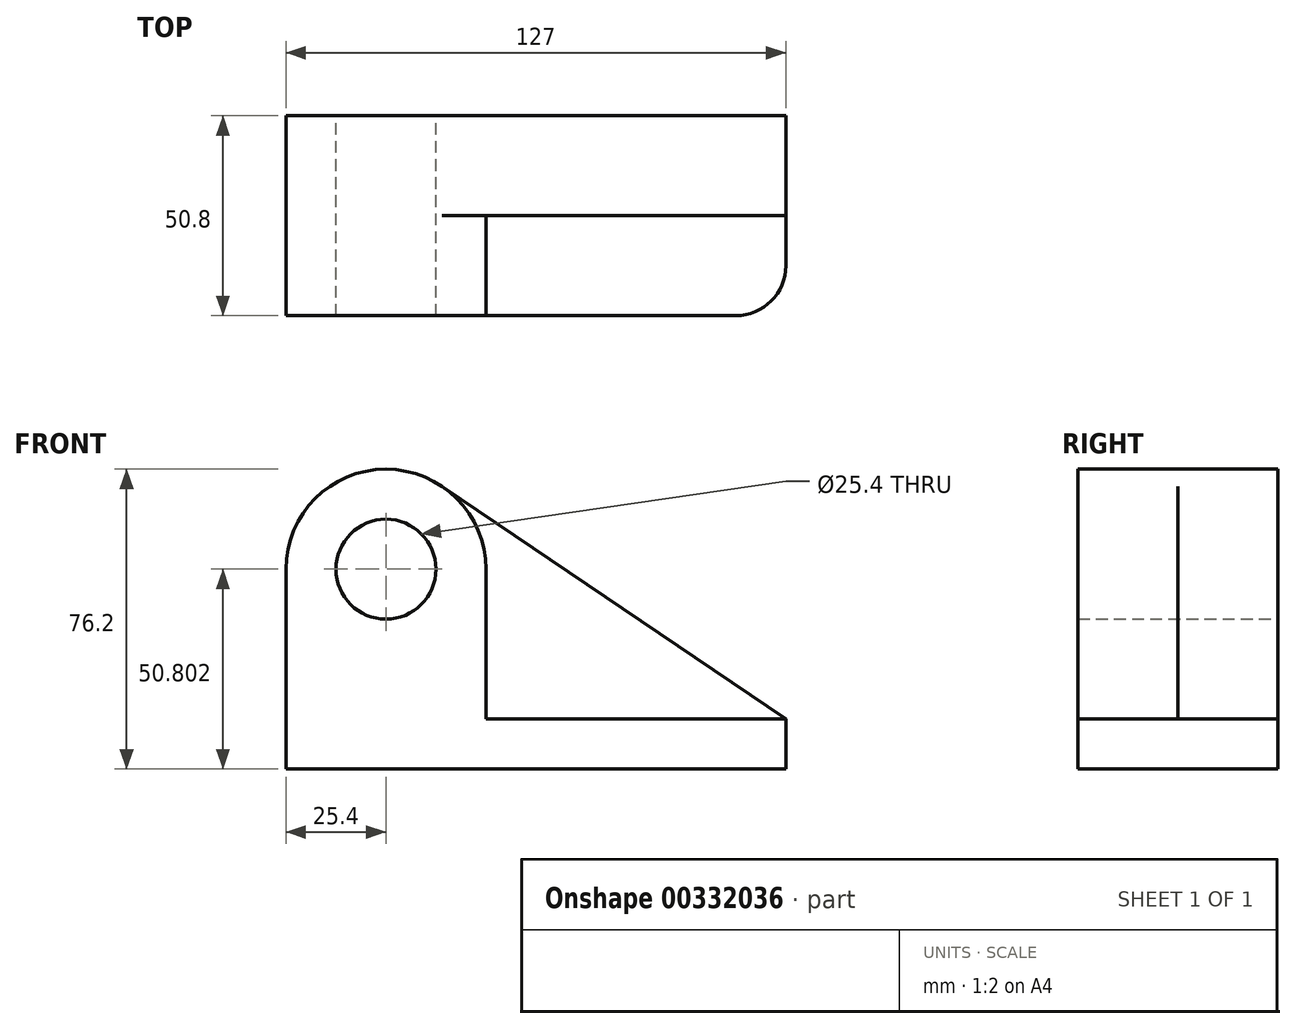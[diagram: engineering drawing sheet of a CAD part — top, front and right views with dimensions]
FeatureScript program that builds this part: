
annotation { "Feature Type Name" : "Feature", "Feature Type Description" : "" }
export const myFeature = defineFeature(function(context is Context, id is Id, definition is map)
    precondition{}
    {
        {
            var Q0;
            Q0=qCreatedBy(makeId("Front.planeOp"),FACE);
            var sketch = newSketch(context, id + "F0", { "sketchPlane" : qUnion([Q0])});
            skCircle(sketch, "E0", {"center": v(-42.13, 39.44) * mm, "radius": 12.7 * mm});
            skArc(sketch, "E1", {"start": v(-27.9, 60.48) * mm, "mid": v(-54.04, 61.88) * mm, "end": v(-67.53, 39.44) * mm});
            skLineSegment(sketch, "E2", {"start": v(-67.53, 39.44) * mm, "end": v(-67.53, -11.36) * mm});
            skLineSegment(sketch, "E3", {"start": v(-67.53, -11.36) * mm, "end": v(59.47, -11.36) * mm});
            skLineSegment(sketch, "E4", {"start": v(59.47, -11.36) * mm, "end": v(59.47, 1.34) * mm});
            skLineSegment(sketch, "E5", {"start": v(59.47, 1.34) * mm, "end": v(-27.9, 60.48) * mm});
            skSolve(sketch);
        }
        {
            var Q0;
            Q0=makeQuery(id+"F0.imprint","IMPRINT",FACE,{"disambiguationData":[TD([[makeQuery(id+"F0.imprint","IMPRINT",EDGE,{"derivedFrom":sQuery(id+"F0.wireOp",EDGE,"E0")}),-1.0]])]});
            extrude(context, id + "F1", {"entities" : qUnion([Q0]), "depth" : 25.4 * mm});
        }
        {
            var Q0;
            Q0=makeQuery(id+"F1.opExtrude","CAP_FACE",FACE,{"disambiguationData":[OSD([sQuery(id+"F0.wireOp",EDGE,"E0"),sQuery(id+"F0.wireOp",EDGE,"E1"),sQuery(id+"F0.wireOp",EDGE,"E2"),sQuery(id+"F0.wireOp",EDGE,"E3"),sQuery(id+"F0.wireOp",EDGE,"E4"),sQuery(id+"F0.wireOp",EDGE,"E5")])],"isStart":false});
            var sketch = newSketch(context, id + "F2", { "sketchPlane" : qUnion([Q0])});
            skCircle(sketch, "E6", {"center": v(-42.13, 39.44) * mm, "radius": 12.7 * mm});
            skArc(sketch, "E7", {"start": v(-16.73, 39.44) * mm, "mid": v(-42.13, 64.84) * mm, "end": v(-67.53, 39.44) * mm});
            skLineSegment(sketch, "E8.bottom", {"start": v(59.47, 1.34) * mm, "end": v(-16.73, 1.34) * mm});
            skLineSegment(sketch, "E8.top", {"start": v(59.47, -11.36) * mm, "end": v(-67.53, -11.36) * mm});
            skLineSegment(sketch, "E8.left", {"start": v(59.47, 1.34) * mm, "end": v(59.47, -11.36) * mm});
            skLineSegment(sketch, "E8.right", {"start": v(-67.53, 1.34) * mm, "end": v(-67.53, -11.36) * mm});
            skLineSegment(sketch, "E9", {"start": v(-67.53, 39.44) * mm, "end": v(-67.53, 1.34) * mm});
            skLineSegment(sketch, "E10", {"start": v(-16.73, 39.44) * mm, "end": v(-16.73, 1.34) * mm});
            skSolve(sketch);
        }
        {
            var Q0;
            Q0=makeQuery(id+"F2.imprint","IMPRINT",FACE,{"disambiguationData":[TD([[makeQuery(id+"F2.imprint","IMPRINT",EDGE,{"derivedFrom":sQuery(id+"F2.wireOp",EDGE,"E6")}),-1.0]])]});
            extrude(context, id + "F3", {"entities" : qUnion([Q0]), "operationType" : NewBodyOperationType.ADD, "depth" : 25.4 * mm});
        }
        {
            var Q0;
            Q0=makeQuery(id+"F3.opExtrude","CAP_EDGE",EDGE,{"disambiguationData":[OSD([sQuery(id+"F2.wireOp",EDGE,"E8.left")])],"isStart":false});
            fillet(context, id + "F4", {"entities" : qUnion([Q0]), "radius" : 12.7 * mm, "tangentPropagation" : true, "allowEdgeOverflow" : false});
        }
    });
